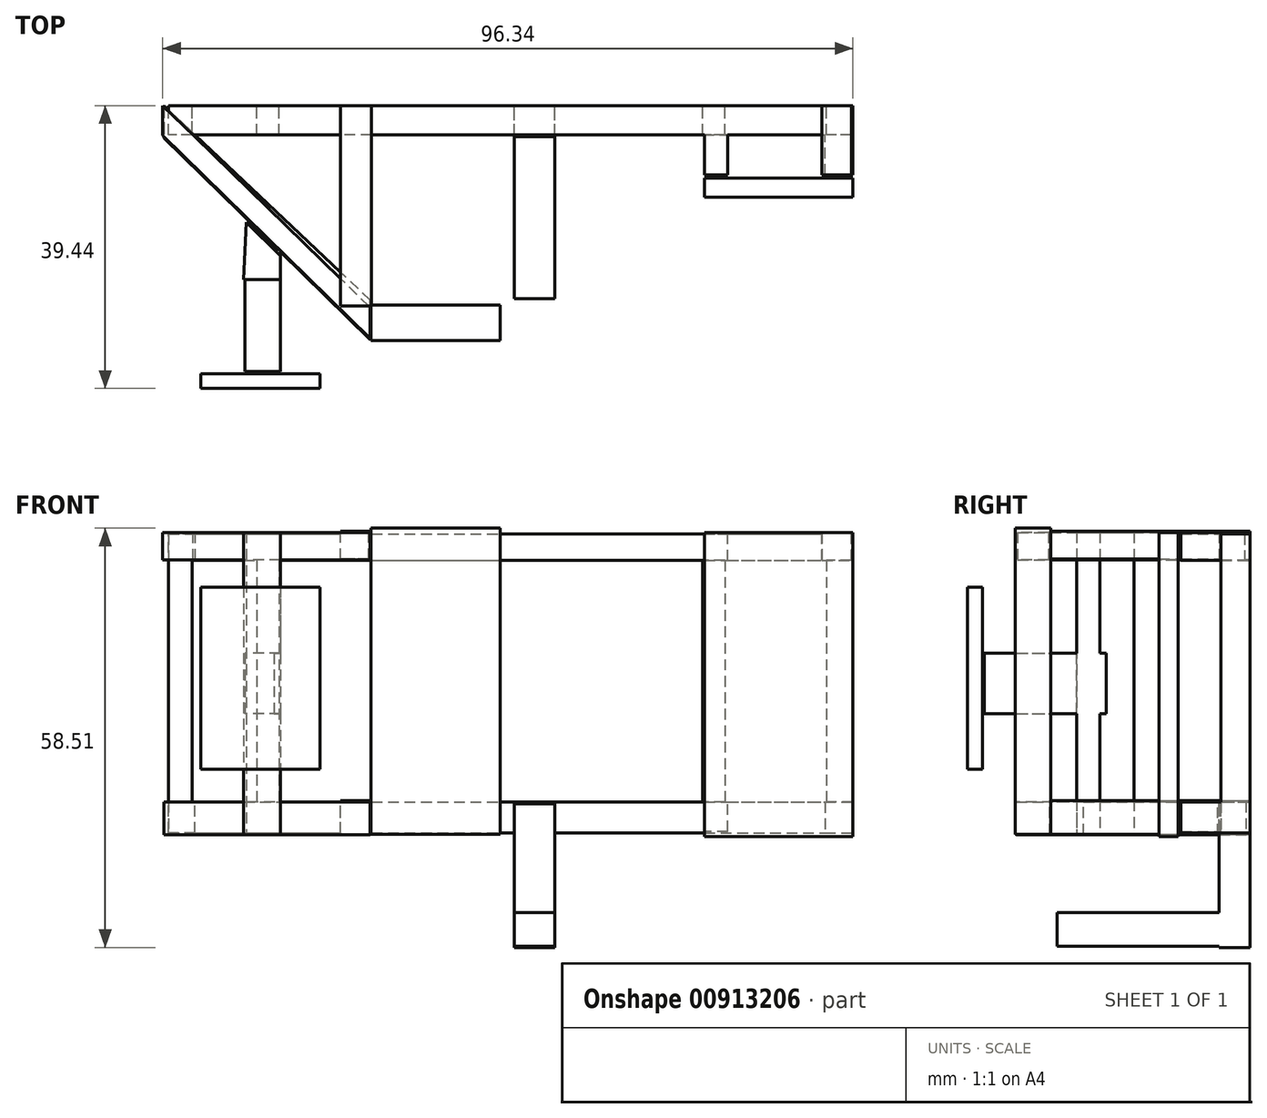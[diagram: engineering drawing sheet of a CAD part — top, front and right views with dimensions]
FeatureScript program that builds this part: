
annotation { "Feature Type Name" : "Feature", "Feature Type Description" : "" }
export const myFeature = defineFeature(function(context is Context, id is Id, definition is map)
    precondition{}
    {
        {
            var Q0;
            Q0=qCreatedBy(makeId("Front.planeOp"),FACE);
            var sketch = newSketch(context, id + "F0", { "sketchPlane" : qUnion([Q0])});
            skLineSegment(sketch, "E0.bottom", {"start": v(-53.92, 0) * mm, "end": v(-50.64, 0) * mm});
            skLineSegment(sketch, "E0.top", {"start": v(-53.92, 17.67) * mm, "end": v(-50.64, 17.67) * mm});
            skLineSegment(sketch, "E0.left", {"start": v(-53.92, 0) * mm, "end": v(-53.92, 17.67) * mm});
            skLineSegment(sketch, "E0.right", {"start": v(-50.64, 0) * mm, "end": v(-50.64, 17.67) * mm});
            skLineSegment(sketch, "E1.bottom", {"start": v(-53.92, 17.67) * mm, "end": v(41.6, 17.67) * mm});
            skLineSegment(sketch, "E1.top", {"start": v(-53.92, 21.36) * mm, "end": v(41.6, 21.36) * mm});
            skLineSegment(sketch, "E1.left", {"start": v(-53.92, 17.67) * mm, "end": v(-53.92, 21.36) * mm});
            skLineSegment(sketch, "E1.right", {"start": v(41.6, 17.67) * mm, "end": v(41.6, 21.36) * mm});
            skLineSegment(sketch, "E2.bottom", {"start": v(41.6, 17.67) * mm, "end": v(37.9, 17.67) * mm});
            skLineSegment(sketch, "E2.top", {"start": v(41.6, 0) * mm, "end": v(37.9, 0) * mm});
            skLineSegment(sketch, "E2.left", {"start": v(41.6, 17.67) * mm, "end": v(41.6, 0) * mm});
            skLineSegment(sketch, "E2.right", {"start": v(37.9, 17.67) * mm, "end": v(37.9, 0) * mm});
            skLineSegment(sketch, "E3.bottom", {"start": v(20.64, 17.67) * mm, "end": v(23.73, 17.67) * mm});
            skLineSegment(sketch, "E3.top", {"start": v(20.64, 0) * mm, "end": v(23.73, 0) * mm});
            skLineSegment(sketch, "E3.left", {"start": v(20.64, 17.67) * mm, "end": v(20.64, 0) * mm});
            skLineSegment(sketch, "E3.right", {"start": v(23.73, 17.67) * mm, "end": v(23.73, 0) * mm});
            skLineSegment(sketch, "E4.bottom", {"start": v(-41.6, 17.67) * mm, "end": v(-38.52, 17.67) * mm});
            skLineSegment(sketch, "E4.top", {"start": v(-41.6, 0) * mm, "end": v(-38.52, 0) * mm});
            skLineSegment(sketch, "E4.left", {"start": v(-41.6, 17.67) * mm, "end": v(-41.6, 0) * mm});
            skLineSegment(sketch, "E4.right", {"start": v(-38.52, 17.67) * mm, "end": v(-38.52, 0) * mm});
            skLineSegment(sketch, "E5.top", {"start": v(-41.6, -16.02) * mm, "end": v(-38.52, -16.02) * mm});
            skLineSegment(sketch, "E5.left", {"start": v(-41.6, 0) * mm, "end": v(-41.6, -16.02) * mm});
            skLineSegment(sketch, "E5.right", {"start": v(-38.52, 0) * mm, "end": v(-38.52, -16.02) * mm});
            skLineSegment(sketch, "E6.top", {"start": v(-53.92, -16.02) * mm, "end": v(-50.64, -16.02) * mm});
            skLineSegment(sketch, "E6.left", {"start": v(-53.92, 0) * mm, "end": v(-53.92, -16.02) * mm});
            skLineSegment(sketch, "E6.right", {"start": v(-50.64, 0) * mm, "end": v(-50.64, -16.02) * mm});
            skLineSegment(sketch, "E7.bottom", {"start": v(20.64, -16.02) * mm, "end": v(23.73, -16.02) * mm});
            skLineSegment(sketch, "E7.left", {"start": v(20.64, -16.02) * mm, "end": v(20.64, 0) * mm});
            skLineSegment(sketch, "E7.right", {"start": v(23.73, -16.02) * mm, "end": v(23.73, 0) * mm});
            skLineSegment(sketch, "E8.bottom", {"start": v(37.9, 0) * mm, "end": v(41.6, 0) * mm});
            skLineSegment(sketch, "E8.top", {"start": v(37.9, -16.02) * mm, "end": v(41.6, -16.02) * mm});
            skLineSegment(sketch, "E8.left", {"start": v(37.9, 0) * mm, "end": v(37.9, -16.02) * mm});
            skLineSegment(sketch, "E8.right", {"start": v(41.6, 0) * mm, "end": v(41.6, -16.02) * mm});
            skLineSegment(sketch, "E9.bottom", {"start": v(-53.92, -16.02) * mm, "end": v(41.6, -16.02) * mm});
            skLineSegment(sketch, "E9.top", {"start": v(-53.92, -20.34) * mm, "end": v(41.6, -20.34) * mm});
            skLineSegment(sketch, "E9.left", {"start": v(-53.92, -16.02) * mm, "end": v(-53.92, -20.34) * mm});
            skLineSegment(sketch, "E9.right", {"start": v(41.6, -16.02) * mm, "end": v(41.6, -20.34) * mm});
            skSolve(sketch);
        }
        {
            var Q0;
            {var subQ5=sQuery(id+"F0.wireOp",EDGE,"E0.top");Q0=makeQuery(id+"F0.imprint","IMPRINT",FACE,{"disambiguationData":[TD([[makeQuery(id+"F0.imprint","IMPRINT",EDGE,{"derivedFrom":subQ5}),1.0]])]});}
            var Q1;
            {var subQ4=sQuery(id+"F0.wireOp",EDGE,"E5.top");Q1=makeQuery(id+"F0.imprint","IMPRINT",FACE,{"disambiguationData":[TD([[makeQuery(id+"F0.imprint","IMPRINT",EDGE,{"derivedFrom":subQ4}),-1.0]])]});}
            var Q2;
            Q2=makeQuery(id+"F0.imprint","IMPRINT",FACE,{"disambiguationData":[TD([[makeQuery(id+"F0.imprint","IMPRINT",EDGE,{"derivedFrom":sQuery(id+"F0.wireOp",EDGE,"E0.bottom")}),-1.0]])]});
            var Q3;
            Q3=makeQuery(id+"F0.imprint","IMPRINT",FACE,{"disambiguationData":[TD([[makeQuery(id+"F0.imprint","IMPRINT",EDGE,{"derivedFrom":sQuery(id+"F0.wireOp",EDGE,"E0.bottom")}),1.0]])]});
            var Q4;
            Q4=makeQuery(id+"F0.imprint","IMPRINT",FACE,{"disambiguationData":[TD([[makeQuery(id+"F0.imprint","IMPRINT",EDGE,{"derivedFrom":sQuery(id+"F0.wireOp",EDGE,"E4.top")}),1.0]])]});
            var Q5;
            Q5=makeQuery(id+"F0.imprint","IMPRINT",FACE,{"disambiguationData":[TD([[makeQuery(id+"F0.imprint","IMPRINT",EDGE,{"derivedFrom":sQuery(id+"F0.wireOp",EDGE,"E4.top")}),-1.0]])]});
            var Q6;
            Q6=makeQuery(id+"F0.imprint","IMPRINT",FACE,{"disambiguationData":[TD([[makeQuery(id+"F0.imprint","IMPRINT",EDGE,{"derivedFrom":sQuery(id+"F0.wireOp",EDGE,"E3.top")}),1.0]])]});
            var Q7;
            Q7=makeQuery(id+"F0.imprint","IMPRINT",FACE,{"disambiguationData":[TD([[makeQuery(id+"F0.imprint","IMPRINT",EDGE,{"derivedFrom":sQuery(id+"F0.wireOp",EDGE,"E3.top")}),-1.0]])]});
            var Q8;
            Q8=makeQuery(id+"F0.imprint","IMPRINT",FACE,{"disambiguationData":[TD([[makeQuery(id+"F0.imprint","IMPRINT",EDGE,{"derivedFrom":sQuery(id+"F0.wireOp",EDGE,"E2.top")}),1.0]])]});
            var Q9;
            Q9=makeQuery(id+"F0.imprint","IMPRINT",FACE,{"disambiguationData":[TD([[makeQuery(id+"F0.imprint","IMPRINT",EDGE,{"derivedFrom":sQuery(id+"F0.wireOp",EDGE,"E2.top")}),-1.0]])]});
            extrude(context, id + "F1", {"entities" : qUnion([Q0, Q1, Q2, Q3, Q4, Q5, Q6, Q7, Q8, Q9]), "depth" : 4.06 * mm, "offsetDistance" : 25.4 * mm});
        }
        {
            var Q0;
            Q0=qCreatedBy(makeId("Front.planeOp"),FACE);
            var sketch = newSketch(context, id + "F2", { "sketchPlane" : qUnion([Q0])});
            skLineSegment(sketch, "E10.bottom", {"start": v(-29.89, 21.77) * mm, "end": v(-25.57, 21.77) * mm});
            skLineSegment(sketch, "E10.top", {"start": v(-29.89, 17.87) * mm, "end": v(-25.57, 17.87) * mm});
            skLineSegment(sketch, "E10.left", {"start": v(-29.89, 21.77) * mm, "end": v(-29.89, 17.87) * mm});
            skLineSegment(sketch, "E10.right", {"start": v(-25.57, 21.77) * mm, "end": v(-25.57, 17.87) * mm});
            skLineSegment(sketch, "E11.bottom", {"start": v(-29.89, -15.82) * mm, "end": v(-25.57, -15.82) * mm});
            skLineSegment(sketch, "E11.top", {"start": v(-29.89, -20.54) * mm, "end": v(-25.57, -20.54) * mm});
            skLineSegment(sketch, "E11.left", {"start": v(-29.89, -15.82) * mm, "end": v(-29.89, -20.54) * mm});
            skLineSegment(sketch, "E11.right", {"start": v(-25.57, -15.82) * mm, "end": v(-25.57, -20.54) * mm});
            skSolve(sketch);
        }
        {
            var Q0;
            Q0=makeQuery(id+"F2.imprint","IMPRINT",FACE,{"disambiguationData":[TD([[makeQuery(id+"F2.imprint","IMPRINT",EDGE,{"derivedFrom":sQuery(id+"F2.wireOp",EDGE,"E11.bottom")}),-1.0]])]});
            var Q1;
            Q1=makeQuery(id+"F2.imprint","IMPRINT",FACE,{"disambiguationData":[TD([[makeQuery(id+"F2.imprint","IMPRINT",EDGE,{"derivedFrom":sQuery(id+"F2.wireOp",EDGE,"E10.bottom")}),-1.0]])]});
            extrude(context, id + "F3", {"entities" : qUnion([Q0, Q1]), "operationType" : NewBodyOperationType.ADD, "depth" : 27.94 * mm, "offsetDistance" : 25.4 * mm});
        }
        {
            var Q0;
            Q0=qCreatedBy(makeId("Top.planeOp"),FACE);
            var sketch = newSketch(context, id + "F4", { "sketchPlane" : qUnion([Q0])});
            skLineSegment(sketch, "E12", {"start": v(-50.22, -4.31) * mm, "end": v(-25.78, -28.14) * mm});
            skLineSegment(sketch, "E13", {"start": v(-25.78, -28.14) * mm, "end": v(-25.78, -32.46) * mm});
            skLineSegment(sketch, "E14", {"start": v(-25.78, -32.46) * mm, "end": v(-54.74, -4.1) * mm});
            skLineSegment(sketch, "E15", {"start": v(-54.74, -4.1) * mm, "end": v(-54.74, 0) * mm});
            skLineSegment(sketch, "E16", {"start": v(-54.74, 0) * mm, "end": v(-50.22, -4.31) * mm});
            skSolve(sketch);
        }
        {
            var Q0;
            Q0=makeQuery(id+"F4.imprint","IMPRINT",FACE,{"disambiguationData":[TD([[makeQuery(id+"F4.imprint","IMPRINT",EDGE,{"derivedFrom":sQuery(id+"F4.wireOp",EDGE,"E12")}),-1.0]])]});
            extrude(context, id + "F5", {"entities" : qUnion([Q0]), "operationType" : NewBodyOperationType.ADD, "depth" : 21.59 * mm, "offsetDistance" : 25.4 * mm, "hasSecondDirection" : true, "secondDirectionOppositeDirection" : false, "secondDirectionDepth" : 17.78 * mm});
        }
        {
            var Q0;
            Q0=qCreatedBy(makeId("Top.planeOp"),FACE);
            var sketch = newSketch(context, id + "F6", { "sketchPlane" : qUnion([Q0])});
            skLineSegment(sketch, "E17", {"start": v(-25.78, -32.66) * mm, "end": v(-25.78, -27.12) * mm});
            skLineSegment(sketch, "E18", {"start": v(-25.78, -27.12) * mm, "end": v(-54.54, 0) * mm});
            skLineSegment(sketch, "E19", {"start": v(-54.54, 0) * mm, "end": v(-54.54, -4.52) * mm});
            skLineSegment(sketch, "E20", {"start": v(-54.54, -4.52) * mm, "end": v(-25.78, -32.66) * mm});
            skSolve(sketch);
        }
        {
            var Q0;
            Q0=makeQuery(id+"F6.imprint","IMPRINT",FACE,{"disambiguationData":[TD([[makeQuery(id+"F6.imprint","IMPRINT",EDGE,{"derivedFrom":sQuery(id+"F6.wireOp",EDGE,"E17")}),1.0]])]});
            extrude(context, id + "F7", {"entities" : qUnion([Q0]), "operationType" : NewBodyOperationType.ADD, "oppositeDirection" : true, "depth" : 20.57 * mm, "offsetDistance" : 25.4 * mm, "hasSecondDirection" : true, "secondDirectionOppositeDirection" : true, "secondDirectionDepth" : 16 * mm});
        }
        {
            var Q0;
            Q0=qCreatedBy(makeId("Right.planeOp"),FACE);
            var sketch = newSketch(context, id + "F8", { "sketchPlane" : qUnion([Q0])});
            skLineSegment(sketch, "E21.bottom", {"start": v(-27.83, 22.19) * mm, "end": v(-32.76, 22.19) * mm});
            skLineSegment(sketch, "E21.top", {"start": v(-27.83, -20.54) * mm, "end": v(-32.76, -20.54) * mm});
            skLineSegment(sketch, "E21.left", {"start": v(-27.83, 22.19) * mm, "end": v(-27.83, -20.54) * mm});
            skLineSegment(sketch, "E21.right", {"start": v(-32.76, 22.19) * mm, "end": v(-32.76, -20.54) * mm});
            skSolve(sketch);
        }
        {
            var Q0;
            Q0=makeQuery(id+"F8.imprint","IMPRINT",FACE,{"disambiguationData":[TD([[makeQuery(id+"F8.imprint","IMPRINT",EDGE,{"derivedFrom":sQuery(id+"F8.wireOp",EDGE,"E21.bottom")}),1.0]])]});
            extrude(context, id + "F9", {"entities" : qUnion([Q0]), "operationType" : NewBodyOperationType.ADD, "oppositeDirection" : true, "depth" : 25.65 * mm, "offsetDistance" : 25.4 * mm, "hasSecondDirection" : true, "secondDirectionOppositeDirection" : true, "secondDirectionDepth" : 7.62 * mm});
        }
        {
            var Q0;
            Q0=qCreatedBy(makeId("Front.planeOp"),FACE);
            var sketch = newSketch(context, id + "F10", { "sketchPlane" : qUnion([Q0])});
            skLineSegment(sketch, "E22.bottom", {"start": v(20.85, 21.36) * mm, "end": v(24.14, 21.36) * mm});
            skLineSegment(sketch, "E22.top", {"start": v(20.85, 17.67) * mm, "end": v(24.14, 17.67) * mm});
            skLineSegment(sketch, "E22.left", {"start": v(20.85, 21.36) * mm, "end": v(20.85, 17.67) * mm});
            skLineSegment(sketch, "E22.right", {"start": v(24.14, 21.36) * mm, "end": v(24.14, 17.67) * mm});
            skLineSegment(sketch, "E23.bottom", {"start": v(20.85, -16.02) * mm, "end": v(24.14, -16.02) * mm});
            skLineSegment(sketch, "E23.top", {"start": v(20.85, -20.13) * mm, "end": v(24.14, -20.13) * mm});
            skLineSegment(sketch, "E23.left", {"start": v(20.85, -16.02) * mm, "end": v(20.85, -20.13) * mm});
            skLineSegment(sketch, "E23.right", {"start": v(24.14, -16.02) * mm, "end": v(24.14, -20.13) * mm});
            skLineSegment(sketch, "E24.bottom", {"start": v(37.7, -20.34) * mm, "end": v(41.6, -20.34) * mm});
            skLineSegment(sketch, "E24.top", {"start": v(37.7, -16.02) * mm, "end": v(41.6, -16.02) * mm});
            skLineSegment(sketch, "E24.left", {"start": v(37.7, -20.34) * mm, "end": v(37.7, -16.02) * mm});
            skLineSegment(sketch, "E24.right", {"start": v(41.6, -20.34) * mm, "end": v(41.6, -16.02) * mm});
            skLineSegment(sketch, "E25.bottom", {"start": v(37.28, 21.57) * mm, "end": v(41.4, 21.57) * mm});
            skLineSegment(sketch, "E25.top", {"start": v(37.28, 17.67) * mm, "end": v(41.4, 17.67) * mm});
            skLineSegment(sketch, "E25.left", {"start": v(37.28, 21.57) * mm, "end": v(37.28, 17.67) * mm});
            skLineSegment(sketch, "E25.right", {"start": v(41.4, 21.57) * mm, "end": v(41.4, 17.67) * mm});
            skSolve(sketch);
        }
        {
            var Q0;
            Q0=makeQuery(id+"F10.imprint","IMPRINT",FACE,{"disambiguationData":[TD([[makeQuery(id+"F10.imprint","IMPRINT",EDGE,{"derivedFrom":sQuery(id+"F10.wireOp",EDGE,"E24.bottom")}),1.0]])]});
            var Q1;
            Q1=makeQuery(id+"F10.imprint","IMPRINT",FACE,{"disambiguationData":[TD([[makeQuery(id+"F10.imprint","IMPRINT",EDGE,{"derivedFrom":sQuery(id+"F10.wireOp",EDGE,"E25.bottom")}),-1.0]])]});
            var Q2;
            Q2=makeQuery(id+"F10.imprint","IMPRINT",FACE,{"disambiguationData":[TD([[makeQuery(id+"F10.imprint","IMPRINT",EDGE,{"derivedFrom":sQuery(id+"F10.wireOp",EDGE,"E22.bottom")}),-1.0]])]});
            var Q3;
            Q3=makeQuery(id+"F10.imprint","IMPRINT",FACE,{"disambiguationData":[TD([[makeQuery(id+"F10.imprint","IMPRINT",EDGE,{"derivedFrom":sQuery(id+"F10.wireOp",EDGE,"E23.bottom")}),-1.0]])]});
            extrude(context, id + "F11", {"entities" : qUnion([Q0, Q1, Q2, Q3]), "operationType" : NewBodyOperationType.ADD, "depth" : 9.65 * mm, "offsetDistance" : 25.4 * mm});
        }
        {
            var Q0;
            Q0=qCreatedBy(makeId("Top.planeOp"),FACE);
            var sketch = newSketch(context, id + "F12", { "sketchPlane" : qUnion([Q0])});
            skLineSegment(sketch, "E26.bottom", {"start": v(20.85, -10.07) * mm, "end": v(41.6, -10.07) * mm});
            skLineSegment(sketch, "E26.top", {"start": v(20.85, -12.74) * mm, "end": v(41.6, -12.74) * mm});
            skLineSegment(sketch, "E26.left", {"start": v(20.85, -10.07) * mm, "end": v(20.85, -12.74) * mm});
            skLineSegment(sketch, "E26.right", {"start": v(41.6, -10.07) * mm, "end": v(41.6, -12.74) * mm});
            skSolve(sketch);
        }
        {
            var Q0;
            Q0=makeQuery(id+"F12.imprint","IMPRINT",FACE,{"disambiguationData":[TD([[makeQuery(id+"F12.imprint","IMPRINT",EDGE,{"derivedFrom":sQuery(id+"F12.wireOp",EDGE,"E26.bottom")}),-1.0]])]});
            extrude(context, id + "F13", {"entities" : qUnion([Q0]), "depth" : 21.59 * mm, "offsetDistance" : 25.4 * mm, "hasSecondDirection" : true, "secondDirectionOppositeDirection" : true, "secondDirectionDepth" : 20.83 * mm});
        }
        {
            var Q0;
            Q0=qCreatedBy(makeId("Top.planeOp"),FACE);
            var sketch = newSketch(context, id + "F14", { "sketchPlane" : qUnion([Q0])});
            skLineSegment(sketch, "E27.bottom", {"start": v(-5.65, -4.31) * mm, "end": v(0, -4.31) * mm});
            skLineSegment(sketch, "E27.top", {"start": v(-5.65, 0) * mm, "end": v(0, 0) * mm});
            skLineSegment(sketch, "E27.left", {"start": v(-5.65, -4.31) * mm, "end": v(-5.65, 0) * mm});
            skLineSegment(sketch, "E27.right", {"start": v(0, -4.31) * mm, "end": v(0, 0) * mm});
            skSolve(sketch);
        }
        {
            var Q0;
            Q0=makeQuery(id+"F14.imprint","IMPRINT",FACE,{"disambiguationData":[TD([[makeQuery(id+"F14.imprint","IMPRINT",EDGE,{"derivedFrom":sQuery(id+"F14.wireOp",EDGE,"E27.bottom")}),1.0]])]});
            extrude(context, id + "F15", {"entities" : qUnion([Q0]), "operationType" : NewBodyOperationType.ADD, "oppositeDirection" : true, "depth" : 36.32 * mm, "offsetDistance" : 25.4 * mm, "hasSecondDirection" : true, "secondDirectionOppositeDirection" : true, "secondDirectionDepth" : 16.26 * mm});
        }
        {
            var Q0;
            Q0=qCreatedBy(makeId("Front.planeOp"),FACE);
            var sketch = newSketch(context, id + "F16", { "sketchPlane" : qUnion([Q0])});
            skLineSegment(sketch, "E28.bottom", {"start": v(-5.65, -31.43) * mm, "end": v(0, -31.43) * mm});
            skLineSegment(sketch, "E28.top", {"start": v(-5.65, -36.15) * mm, "end": v(0, -36.15) * mm});
            skLineSegment(sketch, "E28.left", {"start": v(-5.65, -31.43) * mm, "end": v(-5.65, -36.15) * mm});
            skLineSegment(sketch, "E28.right", {"start": v(0, -31.43) * mm, "end": v(0, -36.15) * mm});
            skSolve(sketch);
        }
        {
            var Q0;
            Q0=makeQuery(id+"F16.imprint","IMPRINT",FACE,{"disambiguationData":[TD([[makeQuery(id+"F16.imprint","IMPRINT",EDGE,{"derivedFrom":sQuery(id+"F16.wireOp",EDGE,"E28.bottom")}),-1.0]])]});
            extrude(context, id + "F17", {"entities" : qUnion([Q0]), "operationType" : NewBodyOperationType.ADD, "depth" : 26.92 * mm, "offsetDistance" : 25.4 * mm});
        }
        {
            var Q0;
            Q0=qCreatedBy(makeId("Top.planeOp"),FACE);
            var sketch = newSketch(context, id + "F18", { "sketchPlane" : qUnion([Q0])});
            skLineSegment(sketch, "E29", {"start": v(-43.03, -16.23) * mm, "end": v(-38.31, -20.95) * mm});
            skLineSegment(sketch, "E30", {"start": v(-38.31, -20.95) * mm, "end": v(-38.31, -24.24) * mm});
            skLineSegment(sketch, "E31", {"start": v(-38.31, -24.24) * mm, "end": v(-43.45, -24.24) * mm});
            skLineSegment(sketch, "E32", {"start": v(-43.45, -24.24) * mm, "end": v(-43.03, -16.23) * mm});
            skSolve(sketch);
        }
        {
            var Q0;
            Q0=makeQuery(id+"F18.imprint","IMPRINT",FACE,{"disambiguationData":[TD([[makeQuery(id+"F18.imprint","IMPRINT",EDGE,{"derivedFrom":sQuery(id+"F18.wireOp",EDGE,"E29")}),-1.0]])]});
            extrude(context, id + "F19", {"entities" : qUnion([Q0]), "depth" : 21.59 * mm, "offsetDistance" : 25.4 * mm, "hasSecondDirection" : true, "secondDirectionOppositeDirection" : true, "secondDirectionDepth" : 20.57 * mm});
        }
        {
            var Q0;
            Q0=qCreatedBy(makeId("Front.planeOp"),FACE);
            var sketch = newSketch(context, id + "F20", { "sketchPlane" : qUnion([Q0])});
            skLineSegment(sketch, "E33.bottom", {"start": v(-43.24, 4.72) * mm, "end": v(-38.31, 4.72) * mm});
            skLineSegment(sketch, "E33.top", {"start": v(-43.24, -3.7) * mm, "end": v(-38.31, -3.7) * mm});
            skLineSegment(sketch, "E33.left", {"start": v(-43.24, 4.72) * mm, "end": v(-43.24, -3.7) * mm});
            skLineSegment(sketch, "E33.right", {"start": v(-38.31, 4.72) * mm, "end": v(-38.31, -3.7) * mm});
            skSolve(sketch);
        }
        {
            var Q0;
            Q0=makeQuery(id+"F20.imprint","IMPRINT",FACE,{"disambiguationData":[TD([[makeQuery(id+"F20.imprint","IMPRINT",EDGE,{"derivedFrom":sQuery(id+"F20.wireOp",EDGE,"E33.bottom")}),-1.0]])]});
            extrude(context, id + "F21", {"entities" : qUnion([Q0]), "operationType" : NewBodyOperationType.ADD, "depth" : 37.08 * mm, "offsetDistance" : 25.4 * mm, "hasSecondDirection" : true, "secondDirectionOppositeDirection" : false, "secondDirectionDepth" : 20.07 * mm});
        }
        {
            var Q0;
            Q0=qCreatedBy(makeId("Top.planeOp"),FACE);
            var sketch = newSketch(context, id + "F22", { "sketchPlane" : qUnion([Q0])});
            skLineSegment(sketch, "E34.bottom", {"start": v(-49.4, -37.39) * mm, "end": v(-32.76, -37.39) * mm});
            skLineSegment(sketch, "E34.top", {"start": v(-49.4, -39.44) * mm, "end": v(-32.76, -39.44) * mm});
            skLineSegment(sketch, "E34.left", {"start": v(-49.4, -37.39) * mm, "end": v(-49.4, -39.44) * mm});
            skLineSegment(sketch, "E34.right", {"start": v(-32.76, -37.39) * mm, "end": v(-32.76, -39.44) * mm});
            skSolve(sketch);
        }
        {
            var Q0;
            Q0=makeQuery(id+"F22.imprint","IMPRINT",FACE,{"disambiguationData":[TD([[makeQuery(id+"F22.imprint","IMPRINT",EDGE,{"derivedFrom":sQuery(id+"F22.wireOp",EDGE,"E34.bottom")}),-1.0]])]});
            extrude(context, id + "F23", {"entities" : qUnion([Q0]), "depth" : 13.97 * mm, "offsetDistance" : 25.4 * mm, "hasSecondDirection" : true, "secondDirectionOppositeDirection" : true, "secondDirectionDepth" : 11.43 * mm});
        }
    });
